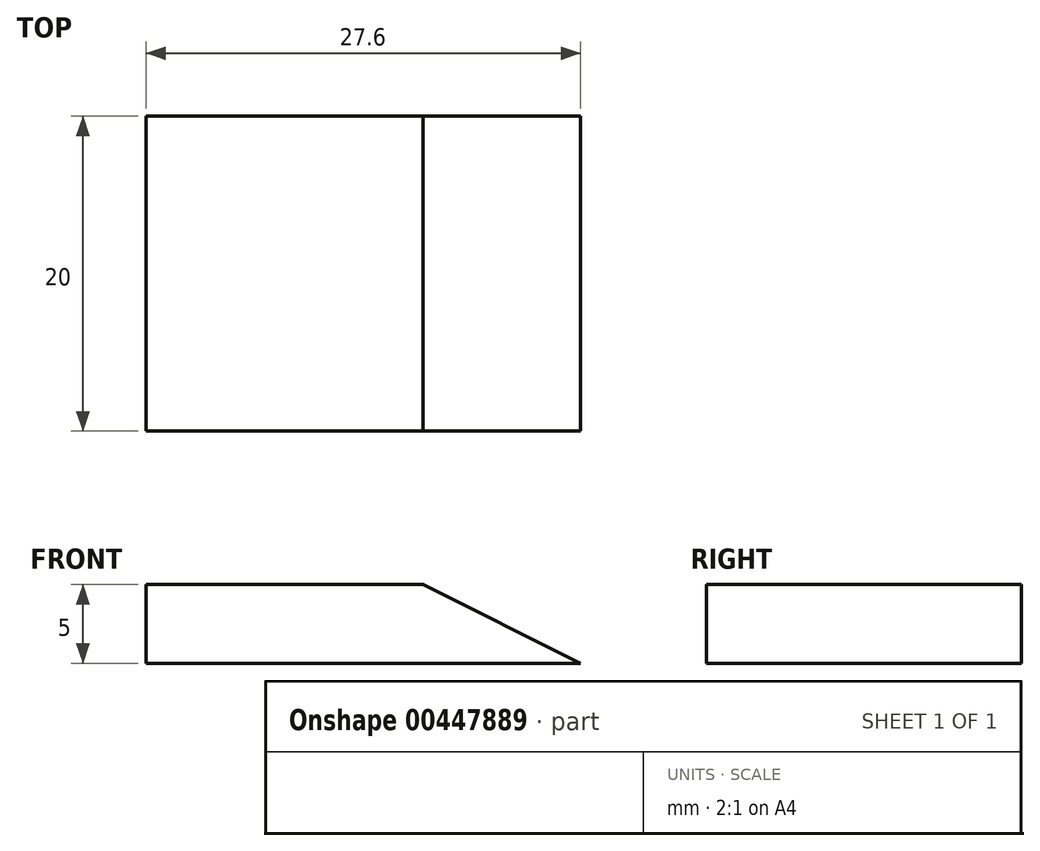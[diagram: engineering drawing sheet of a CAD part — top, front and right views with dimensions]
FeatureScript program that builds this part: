
annotation { "Feature Type Name" : "Feature", "Feature Type Description" : "" }
export const myFeature = defineFeature(function(context is Context, id is Id, definition is map)
    precondition{}
    {
        {
            var Q0;
            Q0=qCreatedBy(makeId("Top.planeOp"),FACE);
            var sketch = newSketch(context, id + "F0", { "sketchPlane" : qUnion([Q0])});
            skPoint(sketch, "E0.middle", {"position": v(0, 0) * mm});
            skLineSegment(sketch, "E1", {"start": v(0, 10) * mm, "end": v(0, -10) * mm});
            skLineSegment(sketch, "E2", {"start": v(0, 10) * mm, "end": v(27.6, 10) * mm});
            skLineSegment(sketch, "E3", {"start": v(0, -10) * mm, "end": v(27.6, -10) * mm});
            skLineSegment(sketch, "E4", {"start": v(27.6, 10) * mm, "end": v(27.6, -10) * mm});
            skSolve(sketch);
        }
        {
            var Q0;
            Q0 = qSketchRegion(id + "F0", true);
            extrude(context, id + "F1", {"entities" : qUnion([Q0]), "depth" : 5 * mm});
        }
        {
            var Q0;
            Q0=makeQuery(id+"F1.opExtrude","SWEPT_FACE",FACE,{"disambiguationData":[OSD([sQuery(id+"F0.wireOp",EDGE,"E3")])]});
            var sketch = newSketch(context, id + "F2", { "sketchPlane" : qUnion([Q0])});
            skPoint(sketch, "E5", {"position": v(17.6, 5) * mm});
            skLineSegment(sketch, "E6", {"start": v(17.6, 5) * mm, "end": v(27.6, 0) * mm});
            skLineSegment(sketch, "E7", {"start": v(27.6, 0) * mm, "end": v(27.6, 5) * mm});
            skLineSegment(sketch, "E8", {"start": v(27.6, 5) * mm, "end": v(17.6, 5) * mm});
            skSolve(sketch);
        }
        {
            var Q0;
            Q0 = qSketchRegion(id + "F2", true);
            extrude(context, id + "F3", {"entities" : qUnion([Q0]), "operationType" : NewBodyOperationType.REMOVE, "endBound" : BoundingType.THROUGH_ALL, "oppositeDirection" : true, "depth" : 25 * mm});
        }
    });
